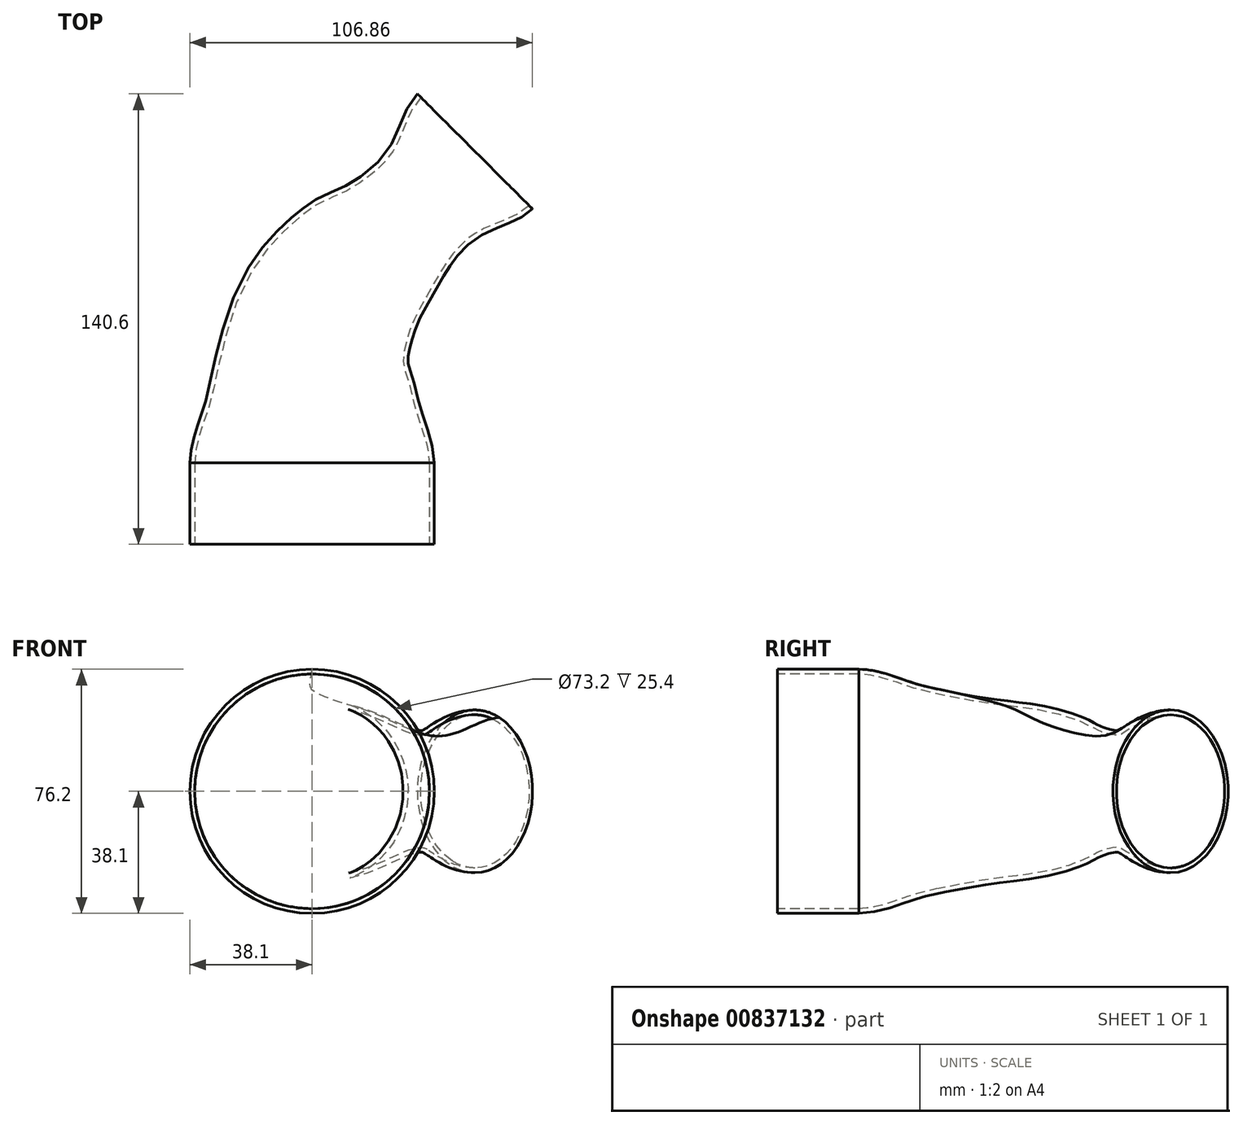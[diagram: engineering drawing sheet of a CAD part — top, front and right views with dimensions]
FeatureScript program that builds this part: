
annotation { "Feature Type Name" : "Feature", "Feature Type Description" : "" }
export const myFeature = defineFeature(function(context is Context, id is Id, definition is map)
    precondition{}
    {
        {
            var Q0;
            Q0=qCreatedBy(makeId("Top.planeOp"),FACE);
            var sketch = newSketch(context, id + "F0", { "sketchPlane" : qUnion([Q0])});
            skLineSegment(sketch, "E0", {"start": v(0, 0) * mm, "end": v(0, 50.8) * mm});
            skArc(sketch, "E1", {"start": v(14.88, 86.72) * mm, "mid": v(3.87, 70.24) * mm, "end": v(0, 50.8) * mm});
            skLineSegment(sketch, "E2", {"start": v(14.88, 86.72) * mm, "end": v(50.8, 122.64) * mm});
            skSolve(sketch);
        }
        {
            var Q0;
            Q0=sQuery(id+"F0.wireOp",EDGE,"E0");
            cPoint(context, id + "F1", {"entities" : qUnion([Q0]), "parameter" : 0.5});
        }
        {
            var Q0;
            Q0=qCreatedBy(makeId("Front.planeOp"),FACE);
            var Q1;
            Q1 = qCreatedBy(id + "F1" ,VERTEX);
            cPlane(context, id + "F2", {"entities" : qUnion([Q0, Q1]), "cplaneType" : CPlaneType.PLANE_POINT, "offset" : 25.4 * mm, "width" : 152.4 * mm, "height" : 152.4 * mm});
        }
        {
            var Q0;
            Q0=qCreatedBy(makeId("Front.planeOp"),FACE);
            var Q1;
            Q1=sQuery(id+"F0.wireOp",VERTEX,"E0.end");
            cPlane(context, id + "F3", {"entities" : qUnion([Q0, Q1]), "cplaneType" : CPlaneType.PLANE_POINT, "offset" : 25.4 * mm, "width" : 152.4 * mm, "height" : 152.4 * mm});
        }
        {
            var Q0;
            Q0=sQuery(id+"F0.wireOp",EDGE,"E1");
            var Q1;
            Q1=sQuery(id+"F0.wireOp",VERTEX,"E1.start");
            cPlane(context, id + "F4", {"entities" : qUnion([Q0, Q1]), "cplaneType" : CPlaneType.CURVE_POINT, "offset" : 25.4 * mm, "width" : 152.4 * mm, "height" : 152.4 * mm});
        }
        {
            var Q0;
            Q0=sQuery(id+"F0.wireOp",EDGE,"E2");
            cPoint(context, id + "F5", {"entities" : qUnion([Q0]), "parameter" : 0.5});
        }
        {
            var Q0;
            Q0=qCreatedBy(id+"F4.planeOp",FACE);
            var Q1;
            Q1 = qCreatedBy(id + "F5" ,VERTEX);
            cPlane(context, id + "F6", {"entities" : qUnion([Q0, Q1]), "cplaneType" : CPlaneType.PLANE_POINT, "offset" : 25.4 * mm, "width" : 152.4 * mm, "height" : 152.4 * mm});
        }
        {
            var Q0;
            Q0=qCreatedBy(id+"F4.planeOp",FACE);
            var Q1;
            Q1=sQuery(id+"F0.wireOp",VERTEX,"E2.end");
            cPlane(context, id + "F7", {"entities" : qUnion([Q0, Q1]), "cplaneType" : CPlaneType.PLANE_POINT, "offset" : 25.4 * mm, "width" : 152.4 * mm, "height" : 152.4 * mm});
        }
        {
            var Q0;
            Q0=qCreatedBy(makeId("Front.planeOp"),FACE);
            var sketch = newSketch(context, id + "F8", { "sketchPlane" : qUnion([Q0])});
            skCircle(sketch, "E3", {"center": v(0, 0) * mm, "radius": 38.1 * mm});
            skSolve(sketch);
        }
        {
            var Q0;
            Q0=qCreatedBy(id+"F2.planeOp",FACE);
            var sketch = newSketch(context, id + "F9", { "sketchPlane" : qUnion([Q0])});
            skCircle(sketch, "E4.0", {"center": v(0, 0) * mm, "radius": 38.1 * mm});
            skSolve(sketch);
        }
        {
            var Q0;
            Q0=qCreatedBy(id+"F3.planeOp",FACE);
            var sketch = newSketch(context, id + "F10", { "sketchPlane" : qUnion([Q0])});
            skCircle(sketch, "E5", {"center": v(0, 0) * mm, "radius": 31.75 * mm});
            skSolve(sketch);
        }
        {
            var Q0;
            Q0=qCreatedBy(id+"F4.planeOp",FACE);
            var sketch = newSketch(context, id + "F11", { "sketchPlane" : qUnion([Q0])});
            skCircle(sketch, "E6", {"center": v(-50.8, 0) * mm, "radius": 25.4 * mm});
            skSolve(sketch);
        }
        {
            var Q0;
            Q0=qCreatedBy(id+"F6.planeOp",FACE);
            var sketch = newSketch(context, id + "F12", { "sketchPlane" : qUnion([Q0])});
            skCircle(sketch, "E7", {"center": v(-50.8, 0) * mm, "radius": 19.05 * mm});
            skSolve(sketch);
        }
        {
            var Q0;
            Q0=qCreatedBy(id+"F7.planeOp",FACE);
            var sketch = newSketch(context, id + "F13", { "sketchPlane" : qUnion([Q0])});
            skCircle(sketch, "E8.0", {"center": v(-50.8, 0) * mm, "radius": 25.4 * mm});
            skSolve(sketch);
        }
        {
            var Q0;
            Q0 = qSketchRegion(id + "F8", true);
            var Q1;
            Q1=sQuery(id+"F9.wireOp",VERTEX,"E4.0.center");
            extrude(context, id + "F14", {"entities" : qUnion([Q0]), "endBound" : BoundingType.UP_TO_VERTEX, "oppositeDirection" : true, "depth" : 25.4 * mm, "endBoundEntityVertex" : qUnion([Q1]), "offsetDistance" : 25.4 * mm});
        }
        {
            var Q0;
            Q0=sQuery(id+"F0.wireOp",EDGE,"E0");
            var Q1;
            Q1=sQuery(id+"F0.wireOp",EDGE,"E1");
            var Q2;
            Q2=sQuery(id+"F0.wireOp",EDGE,"E2");
            var Q3;
            Q3=makeQuery(id+"F14.opExtrude","CAP_FACE",FACE,{"disambiguationData":[OSD([sQuery(id+"F8.wireOp",EDGE,"E3")])],"isStart":false});
            var Q4;
            Q4=makeQuery(id+"F10.imprint","IMPRINT",FACE,{"disambiguationData":[TD([[makeQuery(id+"F10.imprint","IMPRINT",EDGE,{"derivedFrom":sQuery(id+"F10.wireOp",EDGE,"E5")}),1.0]])]});
            var Q5;
            Q5=makeQuery(id+"F11.imprint","IMPRINT",FACE,{"disambiguationData":[TD([[makeQuery(id+"F11.imprint","IMPRINT",EDGE,{"derivedFrom":sQuery(id+"F11.wireOp",EDGE,"E6")}),1.0]])]});
            var Q6;
            Q6=makeQuery(id+"F12.imprint","IMPRINT",FACE,{"disambiguationData":[TD([[makeQuery(id+"F12.imprint","IMPRINT",EDGE,{"derivedFrom":sQuery(id+"F12.wireOp",EDGE,"E7")}),1.0]])]});
            var Q7;
            Q7=makeQuery(id+"F13.imprint","IMPRINT",FACE,{"disambiguationData":[TD([[makeQuery(id+"F13.imprint","IMPRINT",EDGE,{"derivedFrom":sQuery(id+"F13.wireOp",EDGE,"E8.0")}),1.0]])]});
            loft(context, id + "F15", {"operationType" : NewBodyOperationType.ADD, "addSections" : true, "spine" : qUnion([Q0, Q1, Q2]), "sectionCount" : 5, "startCondition" : LoftEndDerivativeType.NORMAL_TO_PROFILE, "startMagnitude" : 1, "endCondition" : LoftEndDerivativeType.NORMAL_TO_PROFILE, "endMagnitude" : 1, "sheetProfilesArray" : [{ "sheetProfileEntities" : qUnion([Q3]) }, { "sheetProfileEntities" : qUnion([Q4]) }, { "sheetProfileEntities" : qUnion([Q5]) }, { "sheetProfileEntities" : qUnion([Q6]) }, { "sheetProfileEntities" : qUnion([Q7]) }]});
        }
        {
            var Q0;
            Q0=makeQuery(id+"F14.opExtrude","CAP_FACE",FACE,{"disambiguationData":[OSD([sQuery(id+"F8.wireOp",EDGE,"E3")])],"isStart":true});
            var Q1;
            Q1=makeQuery(id+"F15.opLoft","CAP_FACE",FACE,{"disambiguationData":[OSD([makeQuery(id+"F13.imprint","IMPRINT",FACE,{"disambiguationData":[TD([[makeQuery(id+"F13.imprint","IMPRINT",EDGE,{"derivedFrom":sQuery(id+"F13.wireOp",EDGE,"E8.0")}),1.0]])]})])],"isStart":true});
            var Q2;
            Q2=makeQuery(id+"F14.opExtrude","SWEPT_BODY",BODY,{"disambiguationData":[OSD([sQuery(id+"F8.wireOp",EDGE,"E3")])]});
            shell(context, id + "F16", {"entities" : qUnion([Q0, Q1]), "parts" : qUnion([Q2]), "thickness" : 1.5 * mm});
        }
    });
